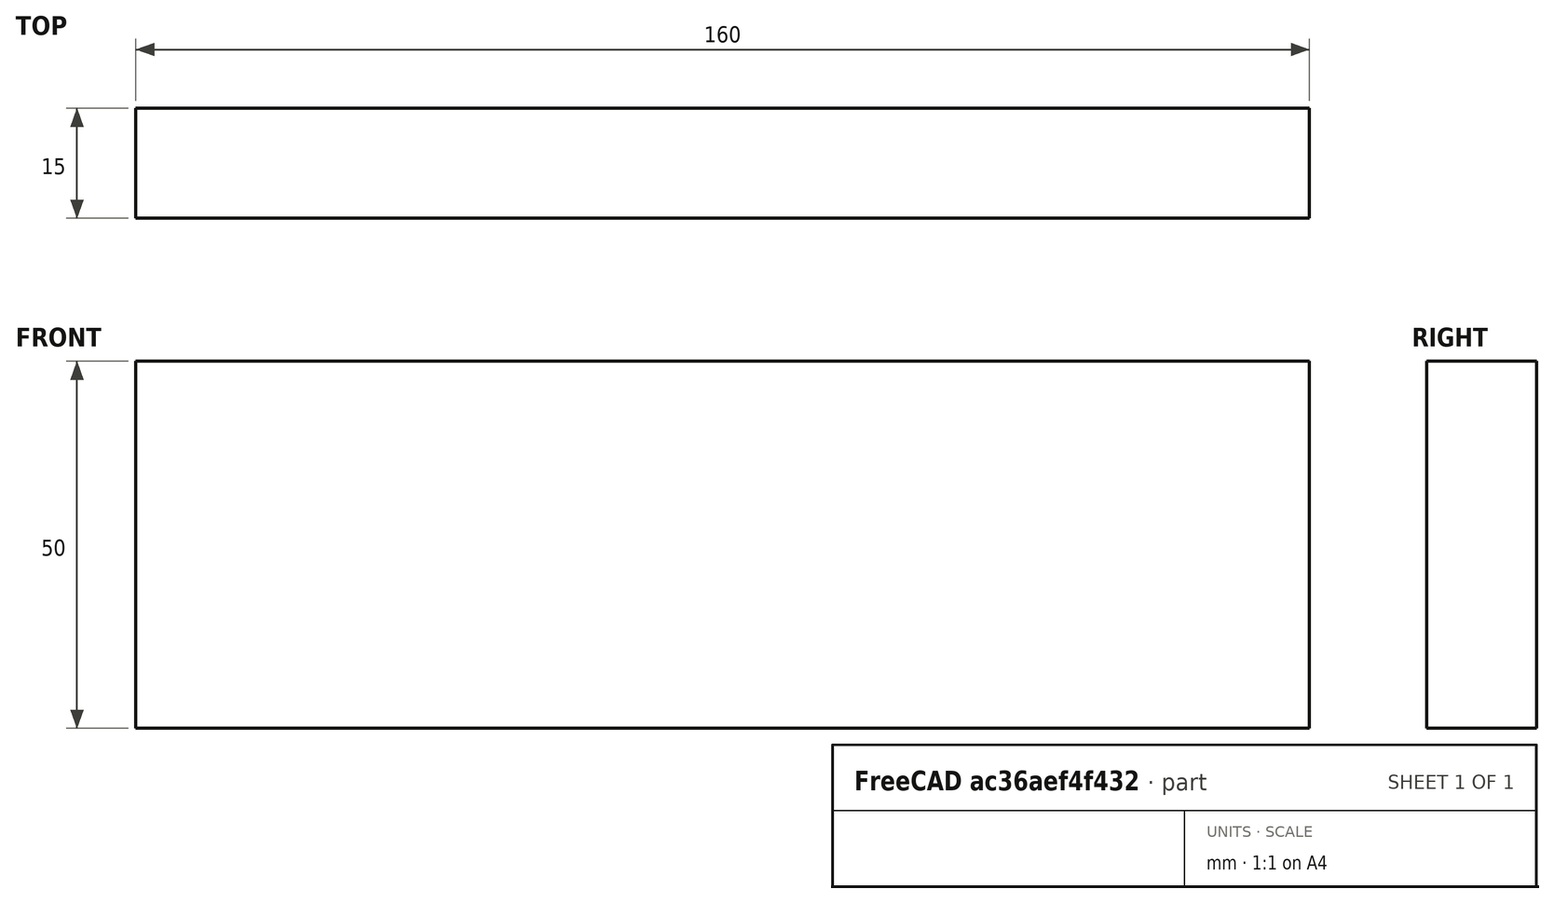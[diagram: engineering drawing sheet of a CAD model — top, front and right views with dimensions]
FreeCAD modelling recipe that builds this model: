
FCSTD DOCUMENT  (FreeCAD 0.15R4671 (Git))
Label: Flat Bar 160x15 EN10058 S235JR
License: All rights reserved
LicenseURL: http://en.wikipedia.org/wiki/All_rights_reserved
objects: Sketcher::SketchObject×1, Part::Extrusion×1
note: 2 computed .brp shape members not serialized (recipe doc carries the construction recipe); baked Part::Feature solids carry a one-line shape summary decoded from their .brp

FEATURE [Sketcher::SketchObject] Sketch
  sketch-geometry (4):
    g0: LineSegment StartX=-80 StartY=-7.5 StartZ=0 EndX=80 EndY=-7.5 EndZ=0
    g1: LineSegment StartX=80 StartY=-7.5 StartZ=0 EndX=80 EndY=7.5 EndZ=0
    g2: LineSegment StartX=80 StartY=7.5 StartZ=0 EndX=-80 EndY=7.5 EndZ=0
    g3: LineSegment StartX=-80 StartY=7.5 StartZ=0 EndX=-80 EndY=-7.5 EndZ=0
  constraints (12):
    c: Coincident(g0,g1)
    c: Coincident(g1,g2)
    c: Coincident(g2,g3)
    c: Coincident(g3,g0)
    c: Horizontal(g0)
    c: Horizontal(g2)
    c: Vertical(g1)
    c: Vertical(g3)
    c: Symmetric(g1,g2,g-2)
    c: Symmetric(g0,g1,g-1)
    c: DistanceY(g1) = 15
    c: DistanceX(g0) = 160
FEATURE [Part::Extrusion] Extrude  label="Flat Bar 160x15 EN10058 S235JR"
  Base = -> Sketch
  Dir = (0,0,50)
  Solid = true
